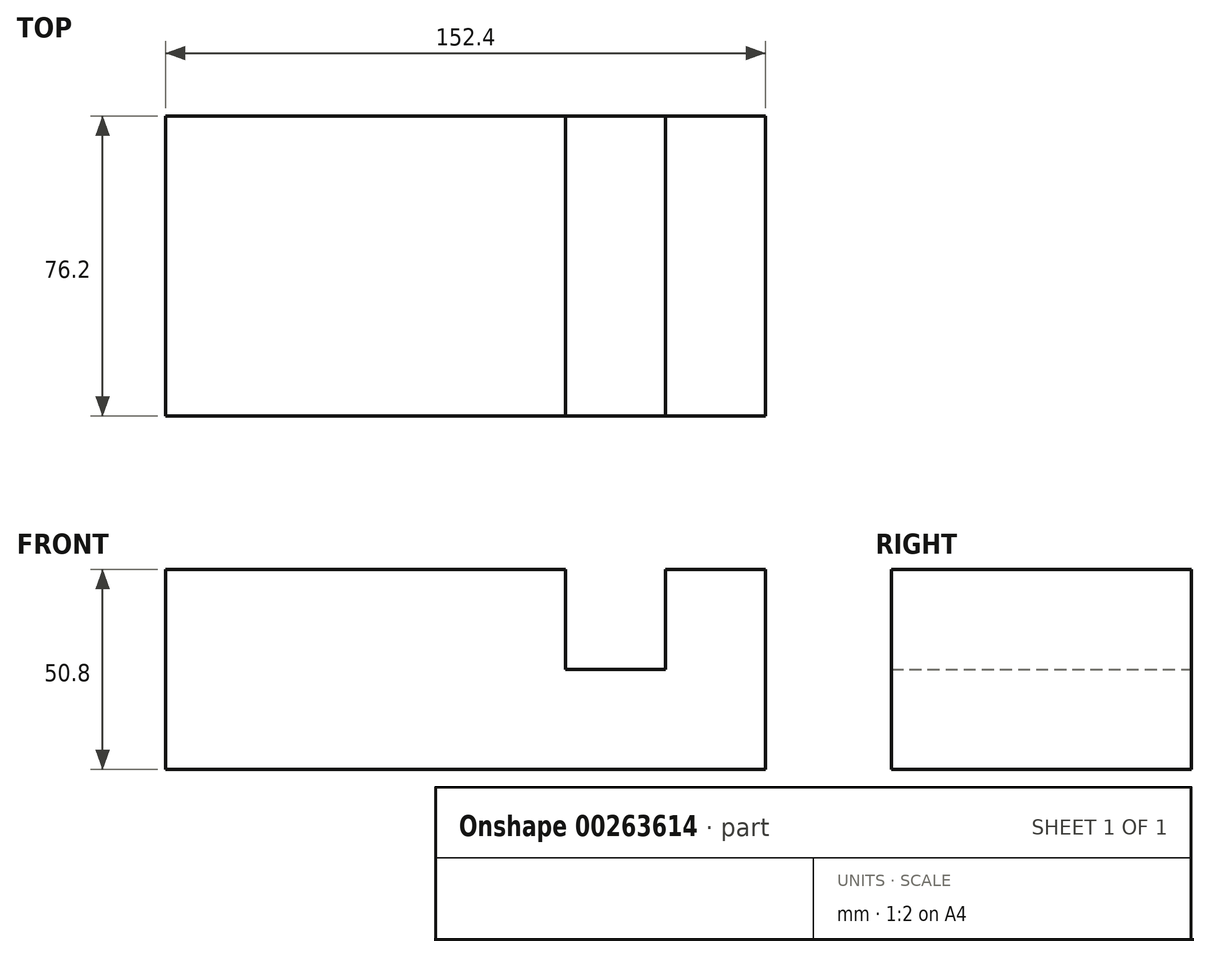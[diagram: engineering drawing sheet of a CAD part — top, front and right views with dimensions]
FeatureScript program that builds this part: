
annotation { "Feature Type Name" : "Feature", "Feature Type Description" : "" }
export const myFeature = defineFeature(function(context is Context, id is Id, definition is map)
    precondition{}
    {
        {
            var Q0;
            Q0=qCreatedBy(makeId("Front.planeOp"),FACE);
            var sketch = newSketch(context, id + "F0", { "sketchPlane" : qUnion([Q0])});
            skLineSegment(sketch, "E0", {"start": v(-91.84, 0) * mm, "end": v(60.56, 0) * mm});
            skLineSegment(sketch, "E1", {"start": v(60.56, 0) * mm, "end": v(60.56, 50.8) * mm});
            skLineSegment(sketch, "E2", {"start": v(60.56, 50.8) * mm, "end": v(35.16, 50.8) * mm});
            skLineSegment(sketch, "E3", {"start": v(35.16, 50.8) * mm, "end": v(35.16, 25.4) * mm});
            skLineSegment(sketch, "E4", {"start": v(35.16, 25.4) * mm, "end": v(9.76, 25.4) * mm});
            skLineSegment(sketch, "E5", {"start": v(9.76, 25.4) * mm, "end": v(9.76, 50.8) * mm});
            skLineSegment(sketch, "E6", {"start": v(9.76, 50.8) * mm, "end": v(-91.84, 50.8) * mm});
            skLineSegment(sketch, "E7", {"start": v(-91.84, 50.8) * mm, "end": v(-91.84, 0) * mm});
            skSolve(sketch);
        }
        {
            var Q0;
            Q0=makeQuery(id+"F0.imprint","IMPRINT",FACE,{"disambiguationData":[TD([[makeQuery(id+"F0.imprint","IMPRINT",EDGE,{"derivedFrom":sQuery(id+"F0.wireOp",EDGE,"E0")}),1.0]])]});
            extrude(context, id + "F1", {"entities" : qUnion([Q0]), "depth" : 76.2 * mm});
        }
    });
